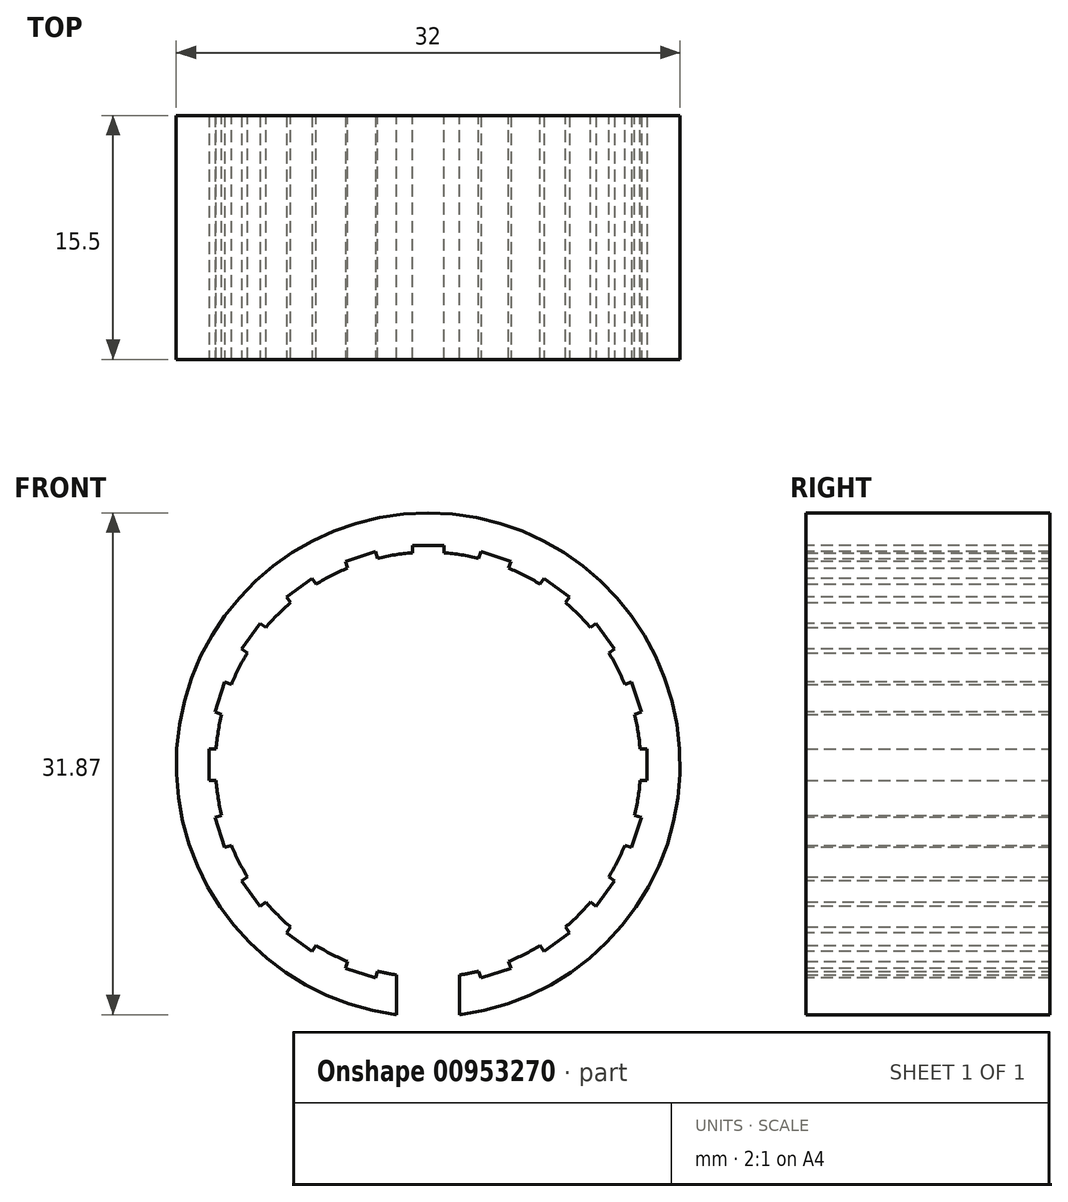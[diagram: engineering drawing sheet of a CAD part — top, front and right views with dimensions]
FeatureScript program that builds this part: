
annotation { "Feature Type Name" : "Feature", "Feature Type Description" : "" }
export const myFeature = defineFeature(function(context is Context, id is Id, definition is map)
    precondition{}
    {
        {
            var Q0;
            Q0=qCreatedBy(makeId("Front.planeOp"),FACE);
            var sketch = newSketch(context, id + "F0", { "sketchPlane" : qUnion([Q0])});
            skCircle(sketch, "E0", {"center": v(0, 0) * mm, "radius": 13.5 * mm});
            skCircle(sketch, "E1", {"center": v(0, 0) * mm, "radius": 16 * mm});
            skSolve(sketch);
        }
        {
            var Q0;
            Q0=qSketchRegion(id+"F0",true);
            extrude(context, id + "F1", {"entities" : qUnion([Q0]), "depth" : 15.5 * mm, "offsetDistance" : 25 * mm});
        }
        {
            var Q0;
            Q0=qCreatedBy(makeId("Top.planeOp"),FACE);
            var sketch = newSketch(context, id + "F2", { "sketchPlane" : qUnion([Q0])});
            skLineSegment(sketch, "E2.bottom", {"start": v(-2, 1.48) * mm, "end": v(2, 1.48) * mm});
            skLineSegment(sketch, "E2.top", {"start": v(-2, -17.61) * mm, "end": v(2, -17.61) * mm});
            skLineSegment(sketch, "E2.left", {"start": v(-2, 1.48) * mm, "end": v(-2, -17.61) * mm});
            skLineSegment(sketch, "E2.right", {"start": v(2, 1.48) * mm, "end": v(2, -17.61) * mm});
            skSolve(sketch);
        }
        {
            var Q0;
            Q0=makeQuery(id+"F2.imprint","IMPRINT",FACE,{"disambiguationData":[TD([[makeQuery(id+"F2.imprint","IMPRINT",EDGE,{"derivedFrom":sQuery(id+"F2.wireOp",EDGE,"E2.bottom")}),-1.0]])]});
            extrude(context, id + "F3", {"entities" : qUnion([Q0]), "operationType" : NewBodyOperationType.REMOVE, "oppositeDirection" : true, "depth" : 25 * mm, "offsetDistance" : 25 * mm});
        }
        {
            var Q0;
            Q0=qCreatedBy(makeId("Front.planeOp"),FACE);
            var sketch = newSketch(context, id + "F4", { "sketchPlane" : qUnion([Q0])});
            skLineSegment(sketch, "E3.bottom", {"start": v(-1, 13.42) * mm, "end": v(1, 13.42) * mm});
            skLineSegment(sketch, "E3.top", {"start": v(-1, 13.92) * mm, "end": v(1, 13.92) * mm});
            skLineSegment(sketch, "E3.left", {"start": v(-1, 13.42) * mm, "end": v(-1, 13.92) * mm});
            skLineSegment(sketch, "E3.right", {"start": v(1, 13.42) * mm, "end": v(1, 13.92) * mm});
            skLineSegment(sketch, "E4.1.0", {"start": v(-5.1, 12.45) * mm, "end": v(-5.25, 12.93) * mm});
            skLineSegment(sketch, "E4.1.1", {"start": v(-5.25, 12.93) * mm, "end": v(-3.35, 13.54) * mm});
            skLineSegment(sketch, "E4.1.2", {"start": v(-3.2, 13.07) * mm, "end": v(-3.35, 13.54) * mm});
            skLineSegment(sketch, "E4.1.3", {"start": v(-5.1, 12.45) * mm, "end": v(-3.2, 13.07) * mm});
            skLineSegment(sketch, "E4.2.0", {"start": v(-8.7, 10.27) * mm, "end": v(-8.99, 10.67) * mm});
            skLineSegment(sketch, "E4.2.1", {"start": v(-8.99, 10.67) * mm, "end": v(-7.37, 11.85) * mm});
            skLineSegment(sketch, "E4.2.2", {"start": v(-7.08, 11.44) * mm, "end": v(-7.37, 11.85) * mm});
            skLineSegment(sketch, "E4.2.3", {"start": v(-8.7, 10.27) * mm, "end": v(-7.08, 11.44) * mm});
            skLineSegment(sketch, "E4.3.0", {"start": v(-11.44, 7.08) * mm, "end": v(-11.85, 7.37) * mm});
            skLineSegment(sketch, "E4.3.1", {"start": v(-11.85, 7.37) * mm, "end": v(-10.67, 8.99) * mm});
            skLineSegment(sketch, "E4.3.2", {"start": v(-10.27, 8.7) * mm, "end": v(-10.67, 8.99) * mm});
            skLineSegment(sketch, "E4.3.3", {"start": v(-11.44, 7.08) * mm, "end": v(-10.27, 8.7) * mm});
            skLineSegment(sketch, "E4.4.0", {"start": v(-13.07, 3.2) * mm, "end": v(-13.54, 3.35) * mm});
            skLineSegment(sketch, "E4.4.1", {"start": v(-13.54, 3.35) * mm, "end": v(-12.93, 5.25) * mm});
            skLineSegment(sketch, "E4.4.2", {"start": v(-12.45, 5.1) * mm, "end": v(-12.93, 5.25) * mm});
            skLineSegment(sketch, "E4.4.3", {"start": v(-13.07, 3.2) * mm, "end": v(-12.45, 5.1) * mm});
            skLineSegment(sketch, "E4.5.0", {"start": v(-13.42, -1) * mm, "end": v(-13.92, -1) * mm});
            skLineSegment(sketch, "E4.5.1", {"start": v(-13.92, -1) * mm, "end": v(-13.92, 1) * mm});
            skLineSegment(sketch, "E4.5.2", {"start": v(-13.42, 1) * mm, "end": v(-13.92, 1) * mm});
            skLineSegment(sketch, "E4.5.3", {"start": v(-13.42, -1) * mm, "end": v(-13.42, 1) * mm});
            skLineSegment(sketch, "E4.6.0", {"start": v(-12.45, -5.1) * mm, "end": v(-12.93, -5.25) * mm});
            skLineSegment(sketch, "E4.6.1", {"start": v(-12.93, -5.25) * mm, "end": v(-13.54, -3.35) * mm});
            skLineSegment(sketch, "E4.6.2", {"start": v(-13.07, -3.2) * mm, "end": v(-13.54, -3.35) * mm});
            skLineSegment(sketch, "E4.6.3", {"start": v(-12.45, -5.1) * mm, "end": v(-13.07, -3.2) * mm});
            skLineSegment(sketch, "E4.7.0", {"start": v(-10.27, -8.7) * mm, "end": v(-10.67, -8.99) * mm});
            skLineSegment(sketch, "E4.7.1", {"start": v(-10.67, -8.99) * mm, "end": v(-11.85, -7.37) * mm});
            skLineSegment(sketch, "E4.7.2", {"start": v(-11.44, -7.08) * mm, "end": v(-11.85, -7.37) * mm});
            skLineSegment(sketch, "E4.7.3", {"start": v(-10.27, -8.7) * mm, "end": v(-11.44, -7.08) * mm});
            skLineSegment(sketch, "E4.8.0", {"start": v(-7.08, -11.44) * mm, "end": v(-7.37, -11.85) * mm});
            skLineSegment(sketch, "E4.8.1", {"start": v(-7.37, -11.85) * mm, "end": v(-8.99, -10.67) * mm});
            skLineSegment(sketch, "E4.8.2", {"start": v(-8.7, -10.27) * mm, "end": v(-8.99, -10.67) * mm});
            skLineSegment(sketch, "E4.8.3", {"start": v(-7.08, -11.44) * mm, "end": v(-8.7, -10.27) * mm});
            skLineSegment(sketch, "E4.9.0", {"start": v(-3.2, -13.07) * mm, "end": v(-3.35, -13.54) * mm});
            skLineSegment(sketch, "E4.9.1", {"start": v(-3.35, -13.54) * mm, "end": v(-5.25, -12.93) * mm});
            skLineSegment(sketch, "E4.9.2", {"start": v(-5.1, -12.45) * mm, "end": v(-5.25, -12.93) * mm});
            skLineSegment(sketch, "E4.9.3", {"start": v(-3.2, -13.07) * mm, "end": v(-5.1, -12.45) * mm});
            skLineSegment(sketch, "E4.10.0", {"start": v(1, -13.42) * mm, "end": v(1, -13.92) * mm});
            skLineSegment(sketch, "E4.10.1", {"start": v(1, -13.92) * mm, "end": v(-1, -13.92) * mm});
            skLineSegment(sketch, "E4.10.2", {"start": v(-1, -13.42) * mm, "end": v(-1, -13.92) * mm});
            skLineSegment(sketch, "E4.10.3", {"start": v(1, -13.42) * mm, "end": v(-1, -13.42) * mm});
            skLineSegment(sketch, "E4.11.0", {"start": v(5.1, -12.45) * mm, "end": v(5.25, -12.93) * mm});
            skLineSegment(sketch, "E4.11.1", {"start": v(5.25, -12.93) * mm, "end": v(3.35, -13.54) * mm});
            skLineSegment(sketch, "E4.11.2", {"start": v(3.2, -13.07) * mm, "end": v(3.35, -13.54) * mm});
            skLineSegment(sketch, "E4.11.3", {"start": v(5.1, -12.45) * mm, "end": v(3.2, -13.07) * mm});
            skLineSegment(sketch, "E4.12.0", {"start": v(8.7, -10.27) * mm, "end": v(8.99, -10.67) * mm});
            skLineSegment(sketch, "E4.12.1", {"start": v(8.99, -10.67) * mm, "end": v(7.37, -11.85) * mm});
            skLineSegment(sketch, "E4.12.2", {"start": v(7.08, -11.44) * mm, "end": v(7.37, -11.85) * mm});
            skLineSegment(sketch, "E4.12.3", {"start": v(8.7, -10.27) * mm, "end": v(7.08, -11.44) * mm});
            skLineSegment(sketch, "E4.13.0", {"start": v(11.44, -7.08) * mm, "end": v(11.85, -7.37) * mm});
            skLineSegment(sketch, "E4.13.1", {"start": v(11.85, -7.37) * mm, "end": v(10.67, -8.99) * mm});
            skLineSegment(sketch, "E4.13.2", {"start": v(10.27, -8.7) * mm, "end": v(10.67, -8.99) * mm});
            skLineSegment(sketch, "E4.13.3", {"start": v(11.44, -7.08) * mm, "end": v(10.27, -8.7) * mm});
            skLineSegment(sketch, "E4.14.0", {"start": v(13.07, -3.2) * mm, "end": v(13.54, -3.35) * mm});
            skLineSegment(sketch, "E4.14.1", {"start": v(13.54, -3.35) * mm, "end": v(12.93, -5.25) * mm});
            skLineSegment(sketch, "E4.14.2", {"start": v(12.45, -5.1) * mm, "end": v(12.93, -5.25) * mm});
            skLineSegment(sketch, "E4.14.3", {"start": v(13.07, -3.2) * mm, "end": v(12.45, -5.1) * mm});
            skLineSegment(sketch, "E4.15.0", {"start": v(13.42, 1) * mm, "end": v(13.92, 1) * mm});
            skLineSegment(sketch, "E4.15.1", {"start": v(13.92, 1) * mm, "end": v(13.92, -1) * mm});
            skLineSegment(sketch, "E4.15.2", {"start": v(13.42, -1) * mm, "end": v(13.92, -1) * mm});
            skLineSegment(sketch, "E4.15.3", {"start": v(13.42, 1) * mm, "end": v(13.42, -1) * mm});
            skLineSegment(sketch, "E4.16.0", {"start": v(12.45, 5.1) * mm, "end": v(12.93, 5.25) * mm});
            skLineSegment(sketch, "E4.16.1", {"start": v(12.93, 5.25) * mm, "end": v(13.54, 3.35) * mm});
            skLineSegment(sketch, "E4.16.2", {"start": v(13.07, 3.2) * mm, "end": v(13.54, 3.35) * mm});
            skLineSegment(sketch, "E4.16.3", {"start": v(12.45, 5.1) * mm, "end": v(13.07, 3.2) * mm});
            skLineSegment(sketch, "E4.17.0", {"start": v(10.27, 8.7) * mm, "end": v(10.67, 8.99) * mm});
            skLineSegment(sketch, "E4.17.1", {"start": v(10.67, 8.99) * mm, "end": v(11.85, 7.37) * mm});
            skLineSegment(sketch, "E4.17.2", {"start": v(11.44, 7.08) * mm, "end": v(11.85, 7.37) * mm});
            skLineSegment(sketch, "E4.17.3", {"start": v(10.27, 8.7) * mm, "end": v(11.44, 7.08) * mm});
            skLineSegment(sketch, "E4.18.0", {"start": v(7.08, 11.44) * mm, "end": v(7.37, 11.85) * mm});
            skLineSegment(sketch, "E4.18.1", {"start": v(7.37, 11.85) * mm, "end": v(8.99, 10.67) * mm});
            skLineSegment(sketch, "E4.18.2", {"start": v(8.7, 10.27) * mm, "end": v(8.99, 10.67) * mm});
            skLineSegment(sketch, "E4.18.3", {"start": v(7.08, 11.44) * mm, "end": v(8.7, 10.27) * mm});
            skLineSegment(sketch, "E4.19.0", {"start": v(3.2, 13.07) * mm, "end": v(3.35, 13.54) * mm});
            skLineSegment(sketch, "E4.19.1", {"start": v(3.35, 13.54) * mm, "end": v(5.25, 12.93) * mm});
            skLineSegment(sketch, "E4.19.2", {"start": v(5.1, 12.45) * mm, "end": v(5.25, 12.93) * mm});
            skLineSegment(sketch, "E4.19.3", {"start": v(3.2, 13.07) * mm, "end": v(5.1, 12.45) * mm});
            skPoint(sketch, "E4.center", {"position": v(0, 0) * mm});
            skSolve(sketch);
        }
        {
            var Q0;
            Q0=qSketchRegion(id+"F4",true);
            extrude(context, id + "F5", {"entities" : qUnion([Q0]), "operationType" : NewBodyOperationType.REMOVE, "endBound" : BoundingType.SYMMETRIC, "oppositeDirection" : true, "depth" : 50 * mm, "offsetDistance" : 25 * mm});
        }
    });
